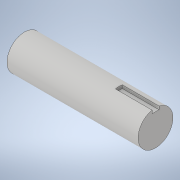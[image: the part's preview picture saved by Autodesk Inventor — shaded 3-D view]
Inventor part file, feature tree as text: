
AUTODESK INVENTOR PART (.ipt)
format: ipt  version: 2021 (Build 250183000, 183)  size: 105,984 bytes
history: native  units: in
note: dims shown in document units (in); Inventor stores cm internally (conversion verified against a paired STEP export)
features: extrude x2, sketch x2, plane x1
ambient origin geometry x8: Origin, YZ Plane, XZ Plane, XY Plane, X Axis, Y Axis, Z Axis, Center Point
bodies: Solid1 (feature_tree)
feature tree (5):
  extrude  "Extrusion1"  Depth=4.69in TaperAngle=0.0deg
  plane  "Work Plane1"
  extrude  "Extrusion9"  Depth=0.25in
  sketch  "Sketch1"  dims[d0=1.25in d1=4.69in d2=0.0in]
  sketch  "Sketch9"  dims[d11=-2.0535in d26=0.25in d27=0.125in d28=1.313in d29=0.0in]
